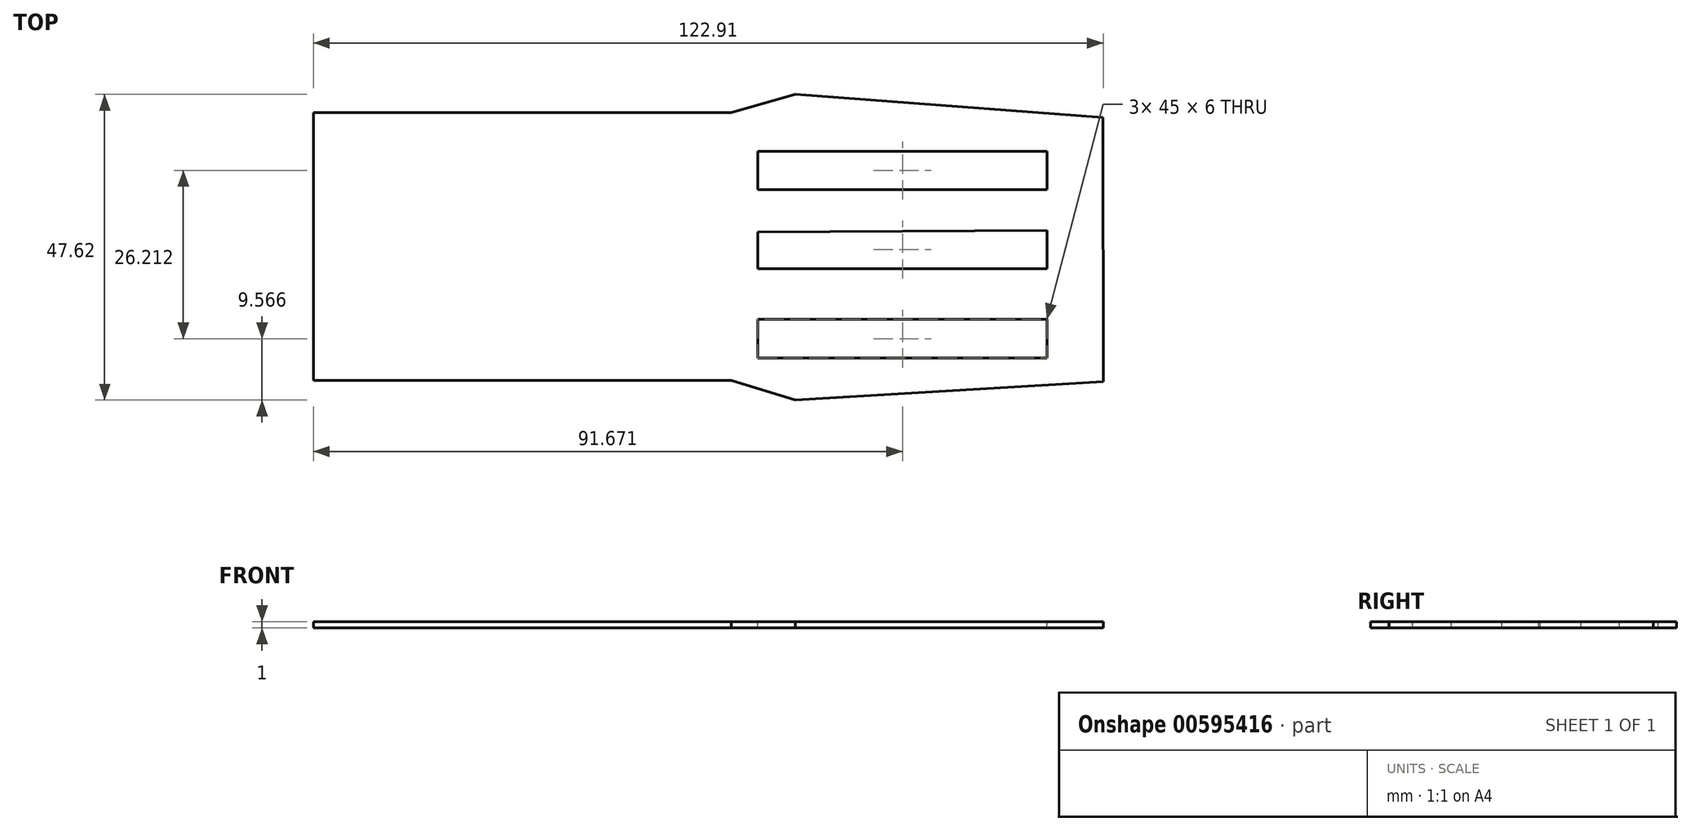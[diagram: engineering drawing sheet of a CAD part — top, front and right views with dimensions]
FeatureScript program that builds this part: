
annotation { "Feature Type Name" : "Feature", "Feature Type Description" : "" }
export const myFeature = defineFeature(function(context is Context, id is Id, definition is map)
    precondition{}
    {
        {
            var Q0;
            Q0=qCreatedBy(makeId("Top.planeOp"),FACE);
            var sketch = newSketch(context, id + "F0", { "sketchPlane" : qUnion([Q0])});
            skLineSegment(sketch, "E0.bottom", {"start": v(75, -49.5) * mm, "end": v(-75, -49.5) * mm});
            skLineSegment(sketch, "E0.top", {"start": v(75, 49.5) * mm, "end": v(-75, 49.5) * mm});
            skLineSegment(sketch, "E0.left", {"start": v(75, -49.5) * mm, "end": v(75, 49.5) * mm});
            skLineSegment(sketch, "E0.right", {"start": v(-75, -49.5) * mm, "end": v(-75, 49.5) * mm});
            skPoint(sketch, "E0.middle", {"position": v(0, 0) * mm});
            skSolve(sketch);
        }
        {
            var Q0;
            Q0=makeQuery(id+"F0.imprint","IMPRINT",FACE,{"disambiguationData":[TD([[makeQuery(id+"F0.imprint","IMPRINT",EDGE,{"derivedFrom":sQuery(id+"F0.wireOp",EDGE,"E0.bottom")}),-1.0]])]});
            extrude(context, id + "F1", {"entities" : qUnion([Q0]), "depth" : 1 * mm, "offsetDistance" : 25 * mm});
        }
        {
            var Q0;
            Q0=makeQuery(id+"F1.opExtrude","CAP_FACE",FACE,{"disambiguationData":[OSD([sQuery(id+"F0.wireOp",EDGE,"E0.bottom"),sQuery(id+"F0.wireOp",EDGE,"E0.top"),sQuery(id+"F0.wireOp",EDGE,"E0.left"),sQuery(id+"F0.wireOp",EDGE,"E0.right")])],"isStart":false});
            var sketch = newSketch(context, id + "F2", { "sketchPlane" : qUnion([Q0])});
            skLineSegment(sketch, "E1", {"start": v(-75, 22.64) * mm, "end": v(-10, 22.64) * mm});
            skLineSegment(sketch, "E2", {"start": v(-75, -19.12) * mm, "end": v(-10, -19.12) * mm});
            skLineSegment(sketch, "E3", {"start": v(-10, 22.64) * mm, "end": v(0, 25.44) * mm});
            skLineSegment(sketch, "E4", {"start": v(-10, -19.12) * mm, "end": v(0, -22.18) * mm});
            skLineSegment(sketch, "E5", {"start": v(0, 25.44) * mm, "end": v(47.87, 21.88) * mm});
            skLineSegment(sketch, "E6", {"start": v(0, -22.18) * mm, "end": v(47.91, -19.27) * mm});
            skLineSegment(sketch, "E7", {"start": v(47.91, -19.27) * mm, "end": v(47.87, 21.88) * mm});
            skLineSegment(sketch, "E8", {"start": v(39.17, 16.6) * mm, "end": v(-5.83, 16.6) * mm});
            skLineSegment(sketch, "E9", {"start": v(-5.83, 16.6) * mm, "end": v(-5.83, 10.6) * mm});
            skLineSegment(sketch, "E10", {"start": v(-5.83, 10.6) * mm, "end": v(39.17, 10.6) * mm});
            skLineSegment(sketch, "E11", {"start": v(39.17, 10.6) * mm, "end": v(39.17, 16.6) * mm});
            skLineSegment(sketch, "E12", {"start": v(39.17, -9.61) * mm, "end": v(39.17, -15.61) * mm});
            skLineSegment(sketch, "E13", {"start": v(39.17, -15.61) * mm, "end": v(-5.83, -15.61) * mm});
            skLineSegment(sketch, "E14", {"start": v(-5.83, -15.61) * mm, "end": v(-5.83, -9.61) * mm});
            skLineSegment(sketch, "E15", {"start": v(-5.83, -9.61) * mm, "end": v(39.17, -9.61) * mm});
            skLineSegment(sketch, "E16", {"start": v(39.17, 4.26) * mm, "end": v(39.17, -1.74) * mm});
            skLineSegment(sketch, "E17", {"start": v(39.17, -1.74) * mm, "end": v(-5.83, -1.74) * mm});
            skLineSegment(sketch, "E18", {"start": v(-5.83, -1.74) * mm, "end": v(-5.83, 4) * mm});
            skLineSegment(sketch, "E19", {"start": v(-5.83, 4) * mm, "end": v(39.17, 4.26) * mm});
            skSolve(sketch);
        }
        {
            var Q0;
            Q0=makeQuery(id+"F2.imprint","IMPRINT",FACE,{"disambiguationData":[TD([[makeQuery(id+"F2.imprint","IMPRINT",EDGE,{"derivedFrom":sQuery(id+"F2.wireOp",EDGE,"E8")}),1.0]])]});
            var Q1;
            Q1=makeQuery(id+"F2.imprint","IMPRINT",FACE,{"disambiguationData":[TD([[makeQuery(id+"F2.imprint","IMPRINT",EDGE,{"derivedFrom":sQuery(id+"F2.wireOp",EDGE,"E16")}),-1.0]])]});
            var Q2;
            Q2=makeQuery(id+"F2.imprint","IMPRINT",FACE,{"disambiguationData":[TD([[makeQuery(id+"F2.imprint","IMPRINT",EDGE,{"derivedFrom":sQuery(id+"F2.wireOp",EDGE,"E12")}),-1.0]])]});
            var Q3;
            {var subQ2=sQuery(id+"F2.wireOp",EDGE,"E1");Q3=makeQuery(id+"F2.imprint","IMPRINT",FACE,{"disambiguationData":[TD([[makeQuery(id+"F2.imprint","IMPRINT",EDGE,{"derivedFrom":subQ2}),1.0]])]});}
            extrude(context, id + "F3", {"entities" : qUnion([Q0, Q1, Q2, Q3]), "operationType" : NewBodyOperationType.REMOVE, "oppositeDirection" : true, "depth" : 25 * mm, "offsetDistance" : 25 * mm});
        }
    });
